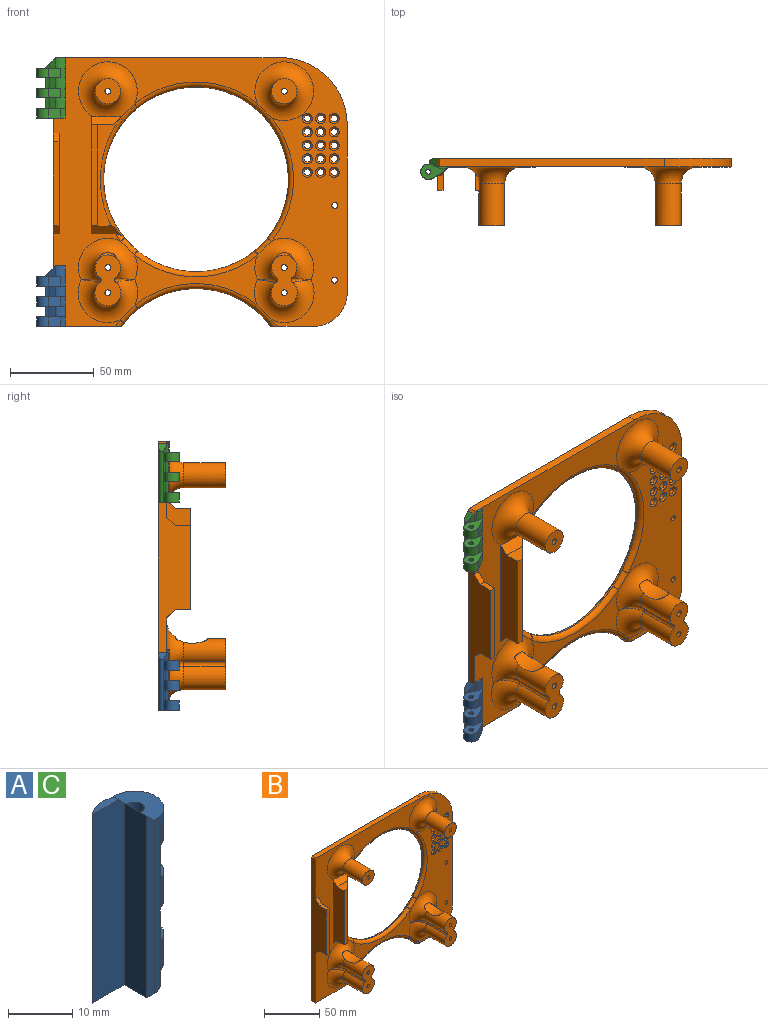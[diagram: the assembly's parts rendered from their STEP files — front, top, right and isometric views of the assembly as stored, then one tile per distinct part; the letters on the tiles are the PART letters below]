
ASSEMBLY  parts=3 mates=2
PART A: 40 faces, bbox 16.8x12.5x36 mm
  f0: plane 34.74x1.74mm, normal (0,-1,0), area 58.9mm2, adj f3,f29,f38,f39
  f1: plane 5.7x2.5mm, normal (-0.71,0.71,0), area 20.2mm2, adj f18,f22,f36,f37
  f2: plane 5.7x2.5mm, normal (-0.71,0.71,0), area 20.2mm2, adj f21,f26,f34,f37
  f3: plane 16.84x12.5mm, normal (0,0,-1), area 102.7mm2, adj f0,f8,f9,f10,f11,f12,f30,f35
  f4: cylinder r=1.5mm len=5.7mm, axis (0,0,1), area 53.7mm2, adj f18,f22
  f5: cylinder r=4.5mm len=9mm, axis (0,0,1), area 94mm2, adj f15,f16,f18,f22
  f6: cylinder r=1.5mm len=5.7mm, axis (0,0,1), area 53.7mm2, adj f21,f26
  f7: cylinder r=4.5mm len=9mm, axis (0,0,1), area 94mm2, adj f13,f14,f21,f26
  f8: cylinder r=1.5mm len=5.7mm, axis (0,0,1), area 53.7mm2, adj f3,f25
  f9: cylinder r=4.5mm len=9mm, axis (0,0,1), area 94mm2, adj f3,f10,f11,f25
  f10: plane 7.27x5.7mm, normal (-0.5,0.87,0), area 47.8mm2, adj f3,f9,f25,f35
  f11: plane 5.7x0.6mm, normal (0,-1,0), area 3.4mm2, adj f3,f9,f12,f25
  f12: plane 30x0.5mm, normal (1,0,0), area 10.6mm2, adj f3,f11,f14,f16,f18,f19,f21,f22
  f13: plane 7.27x5.7mm, normal (-0.5,0.87,0), area 47.8mm2, adj f7,f21,f26,f34
  f14: plane 5.7x0.6mm, normal (0,-1,0), area 3.4mm2, adj f7,f12,f21,f26
  f15: plane 7.27x5.7mm, normal (-0.5,0.87,0), area 47.8mm2, adj f5,f18,f22,f36
  f16: plane 5.7x0.6mm, normal (0,-1,0), area 3.4mm2, adj f5,f12,f18,f22
  f17: plane 5.74x1.45mm, normal (0,0,1), area 6.4mm2, adj f20,f29,f31,f37
  f18: plane 16.84x9.34mm, normal (0,0,1), area 77.8mm2, adj f1,f4,f5,f12,f15,f16,f19,f20
  f19: cylinder r=4.88mm len=2.89mm, axis (0,0,1), area 4.8mm2, adj f12,f18,f20,f29
  f20: plane 6.3x3.46mm, normal (0.43,0.9,0), area 17.8mm2, adj f17,f18,f19,f29,f31
  f21: plane 16.84x9.34mm, normal (0,0,1), area 77.8mm2, adj f2,f6,f7,f12,f13,f14,f23,f24
  f22: plane 16.84x9.34mm, normal (0,0,-1), area 77.8mm2, adj f1,f4,f5,f12,f15,f16,f23,f24
  f23: cylinder r=4.88mm len=6.3mm, axis (0,0,1), area 18.1mm2, adj f12,f21,f22,f24
  f24: plane 6.3x3.46mm, normal (0.43,0.9,0), area 24.2mm2, adj f21,f22,f23,f32
  f25: plane 16.84x9.34mm, normal (0,0,1), area 77.8mm2, adj f8,f9,f10,f11,f12,f27,f28,f30
  f26: plane 16.84x9.34mm, normal (0,0,-1), area 77.8mm2, adj f2,f6,f7,f12,f13,f14,f27,f28
  f27: cylinder r=4.88mm len=6.3mm, axis (0,0,1), area 18.1mm2, adj f12,f25,f26,f28
  f28: plane 6.3x3.46mm, normal (0.43,0.9,0), area 24.2mm2, adj f25,f26,f27,f33
  f29: plane 6x6mm, normal (0.71,0,0.71), area 26.2mm2, adj f0,f12,f17,f19,f20,f37,f38,f39
  f30: plane 5.7x2.5mm, normal (-0.71,0.71,0), area 20.2mm2, adj f3,f25,f35,f37
  f31: cylinder r=5mm len=6.3mm, axis (0,0,1), area 38.7mm2, adj f17,f18,f20,f37
  f32: cylinder r=5mm len=6.3mm, axis (0,0,1), area 38.7mm2, adj f21,f22,f24,f37
  f33: cylinder r=5mm len=6.3mm, axis (0,0,1), area 38.7mm2, adj f25,f26,f28,f37
  f34: cylinder r=5mm len=5.7mm, axis (0,0,-1), area 2.1mm2, adj f2,f13,f21,f26
  f35: cylinder r=5mm len=5.7mm, axis (0,0,-1), area 2.1mm2, adj f3,f10,f25,f30
  f36: cylinder r=5mm len=5.7mm, axis (0,0,-1), area 2.1mm2, adj f1,f15,f18,f22
  f37: plane 36x7mm, normal (0,-1,0), area 251.2mm2, adj f1,f2,f3,f17,f29,f30,f31,f32
  f38: plane 34.74x5mm, normal (-1,0,0), area 173.7mm2, adj f0,f3,f29,f37
  f39: cylinder r=3mm len=33mm, axis (0,0,1), area 146.5mm2, adj f0,f3,f12,f29
PART B: 137 faces, bbox 175.8x40.9x174.3 mm
  f0: plane 175x160mm, normal (0,-1,0), area 8412.6mm2, adj f1,f2,f4,f5,f12,f13,f14,f44
  f1: plane 26.39x5.76mm, normal (0,0,-1), area 125.2mm2, adj f0,f15,f56,f80,f85,f88
  f2: plane 41.39x5.76mm, normal (0,0,-1), area 200.1mm2, adj f0,f12,f15,f56,f84,f85
  f3: plane 73.5x29.9mm, normal (0,-1,0), area 825.3mm2, adj f60,f61,f62,f63,f74,f82
  f4: cylinder r=1.75mm len=3.5mm, axis (0,1,0), area 22mm2, adj f0,f40
  f5: cylinder r=1.75mm len=3.5mm, axis (0,1,0), area 22mm2, adj f0,f38
  f6: cylinder r=1.75mm len=22mm, axis (0,1,0), area 241.9mm2, adj f25,f36
  f7: cylinder r=1.75mm len=22mm, axis (0,1,0), area 241.9mm2, adj f23,f34
  f8: cylinder r=1.75mm len=22mm, axis (0,1,0), area 241.9mm2, adj f19,f32
  f9: cylinder r=1.75mm len=22mm, axis (0,1,0), area 241.9mm2, adj f19,f30
  f10: cylinder r=1.75mm len=22mm, axis (0,1,0), area 241.9mm2, adj f16,f28
  f11: cylinder r=1.75mm len=22mm, axis (0,1,0), area 241.9mm2, adj f16,f26
  f12: plane 158.75x19mm, normal (-1,0,0), area 1518.8mm2, adj f0,f2,f15,f42,f43,f45,f52,f54
  f13: plane 100x5mm, normal (1,0,0), area 500mm2, adj f0,f15,f87,f88
  f14: plane 133.75x5mm, normal (0,0,1), area 668.8mm2, adj f0,f15,f87,f89
  f15: plane 175x160mm, normal (0,1,0), area 15565.5mm2, adj f1,f2,f12,f13,f14,f27,f29,f31
  f16: plane 30.25x15.5mm, normal (0,-1,0), area 350.7mm2, adj f10,f11,f17,f18,f69,f71
  f17: cylinder r=7.75mm len=25mm, axis (0,1,0), area 958.9mm2, adj f16,f60,f69,f71
  f18: cylinder r=7.5mm len=25mm, axis (0,1,0), area 763.3mm2, adj f16,f61,f69,f71,f136
  f19: plane 30.25x15.5mm, normal (0,-1,0), area 350.7mm2, adj f8,f9,f20,f21,f65,f67
  f20: cylinder r=7.75mm len=25mm, axis (0,1,0), area 958.9mm2, adj f19,f62,f65,f67
  f21: cylinder r=7.5mm len=25mm, axis (0,1,0), area 763.3mm2, adj f19,f63,f65,f67,f135
  f22: cylinder r=7.5mm len=25mm, axis (0,1,0), area 1178.1mm2, adj f23,f59
  f23: plane 15x15mm, normal (0,-1,0), area 167.1mm2, adj f7,f22
  f24: cylinder r=7.5mm len=25mm, axis (0,1,0), area 1178.1mm2, adj f25,f58
  f25: plane 15x15mm, normal (0,-1,0), area 167.1mm2, adj f6,f24
  f26: plane 6x6mm, normal (0,1,0), area 18.7mm2, adj f11,f27
  f27: cylinder r=3mm len=18mm, axis (0,1,0), area 339.3mm2, adj f15,f26
  f28: plane 6x6mm, normal (0,1,0), area 18.7mm2, adj f10,f29
  f29: cylinder r=3mm len=18mm, axis (0,1,0), area 339.3mm2, adj f15,f28
  f30: plane 6x6mm, normal (0,1,0), area 18.7mm2, adj f9,f31
  f31: cylinder r=3mm len=18mm, axis (0,1,0), area 339.3mm2, adj f15,f30
  f32: plane 6x6mm, normal (0,1,0), area 18.7mm2, adj f8,f33
  f33: cylinder r=3mm len=18mm, axis (0,1,0), area 339.3mm2, adj f15,f32
  f34: plane 6x6mm, normal (0,1,0), area 18.7mm2, adj f7,f35
  f35: cylinder r=3mm len=18mm, axis (0,1,0), area 339.3mm2, adj f15,f34
  f36: plane 6x6mm, normal (0,1,0), area 18.7mm2, adj f6,f37
  f37: cylinder r=3mm len=18mm, axis (0,1,0), area 339.3mm2, adj f15,f36
  f38: plane 6x6mm, normal (0,1,0), area 18.7mm2, adj f5,f39
  f39: cylinder r=3mm len=6mm, axis (0,1,0), area 56.5mm2, adj f15,f38
  f40: plane 6x6mm, normal (0,1,0), area 18.7mm2, adj f4,f41
  f41: cylinder r=3mm len=6mm, axis (0,1,0), area 56.5mm2, adj f15,f40
  f42: plane 9x3.5mm, normal (0,0,1), area 31.5mm2, adj f12,f44,f45,f52
  f43: plane 9x3.5mm, normal (0,0,-1), area 31.5mm2, adj f12,f44,f45,f54
  f44: plane 60x14mm, normal (1,0,0), area 725mm2, adj f0,f42,f43,f45,f52,f54
  f45: plane 50x3.5mm, normal (0,-1,0), area 175mm2, adj f12,f42,f43,f44
  f46: plane 13.07x9mm, normal (0,0,1), area 77.2mm2, adj f47,f49,f50,f53
  f47: plane 70x14mm, normal (-1,0,0), area 865mm2, adj f0,f46,f48,f49,f51,f53
  f48: plane 12.92x9.02mm, normal (0,0,-1), area 77.1mm2, adj f47,f49,f50,f51,f57
  f49: plane 60x4.07mm, normal (0,-1,0), area 244.3mm2, adj f46,f47,f48,f50
  f50: plane 64.99x13.99mm, normal (0.71,-0.71,0), area 340.1mm2, adj f46,f48,f49,f53,f57,f58
  f51: plane 18.25x6.34mm, normal (0,-0.71,-0.71), area 107.2mm2, adj f0,f47,f48,f57,f72
  f52: plane 5x5mm, normal (0,-0.71,0.71), area 24.7mm2, adj f0,f12,f42,f44
  f53: plane 18.06x5mm, normal (0,-0.71,0.71), area 106.6mm2, adj f0,f46,f47,f50,f58
  f54: plane 5x5mm, normal (0,-0.71,-0.71), area 24.7mm2, adj f0,f12,f43,f44
  f55: cylinder r=55mm len=110mm, axis (0,1,0), area 812.8mm2, adj f57,f72,f73,f74,f75,f76,f77,f78
  f56: cylinder r=55mm len=88.74mm, axis (0,1,0), area 103.2mm2, adj f1,f2,f80,f81,f82,f83,f84,f85
  f57: bspline ~73.3x17.56mm, area 425.2mm2, adj f48,f50,f51,f55,f58,f72,f79
  f58: torus R=17.5mm, axis (0,-1,0), area 1063.5mm2, adj f0,f24,f50,f53,f57,f79
  f59: torus R=17.5mm, axis (0,-1,0), area 1098.9mm2, adj f0,f22,f77
  f60: torus R=17.75mm, axis (0,-1,0), area 792.4mm2, adj f0,f3,f17,f68,f70,f83
  f61: torus R=17.5mm, axis (0,-1,0), area 716.8mm2, adj f0,f3,f18,f68,f70,f73,f136
  f62: torus R=17.75mm, axis (0,-1,0), area 792.4mm2, adj f0,f3,f20,f64,f66,f81
  f63: torus R=17.5mm, axis (0,-1,0), area 716.8mm2, adj f0,f3,f21,f64,f66,f75,f135
  f64: bspline ~13.11x10.57mm, area 21.9mm2, adj f62,f63,f65
  f65: cylinder r=2mm len=25mm, axis (0,-1,0), area 89.3mm2, adj f19,f20,f21,f64
  f66: bspline ~13.11x10.57mm, area 21.9mm2, adj f62,f63,f67
  f67: cylinder r=2mm len=25mm, axis (0,-1,0), area 89.3mm2, adj f19,f20,f21,f66
  f68: bspline ~13.11x10.57mm, area 21.9mm2, adj f60,f61,f69
  f69: cylinder r=2mm len=25mm, axis (0,-1,0), area 89.3mm2, adj f16,f17,f18,f68
  f70: bspline ~13.11x10.57mm, area 21.9mm2, adj f60,f61,f71
  f71: cylinder r=2mm len=25mm, axis (0,-1,0), area 89.3mm2, adj f16,f17,f18,f70
  f72: torus R=58mm, axis (0,-1,0), area 17.6mm2, adj f0,f51,f55,f57,f73
  f73: bspline ~13.46x13.31mm, area 50.2mm2, adj f55,f61,f72,f74
  f74: torus R=58mm, axis (0,-1,0), area 362.8mm2, adj f3,f55,f73,f75
  f75: bspline ~13.46x13.31mm, area 50.2mm2, adj f55,f63,f74,f76
  f76: torus R=58mm, axis (0,-1,0), area 362.8mm2, adj f0,f55,f75,f77
  f77: bspline ~13.46x13.31mm, area 50.2mm2, adj f55,f59,f76,f78
  f78: torus R=58mm, axis (0,-1,0), area 362.8mm2, adj f0,f55,f77,f79
  f79: bspline ~16.65x15.67mm, area 62.6mm2, adj f55,f57,f58,f78
  f80: torus R=58mm, axis (0,-1,0), area 16.7mm2, adj f0,f1,f56,f81
  f81: bspline ~14.19x14.19mm, area 54.8mm2, adj f56,f62,f80,f82
  f82: torus R=58mm, axis (0,-1,0), area 357.6mm2, adj f3,f56,f81,f83
  f83: bspline ~14.19x14.19mm, area 54.8mm2, adj f56,f60,f82,f84
  f84: torus R=58mm, axis (0,-1,0), area 16.7mm2, adj f0,f2,f56,f83
  f85: cone r=55mm half-angle=45deg, axis (0,1,0), area 148.4mm2, adj f1,f2,f15,f56
  f86: cone r=55mm half-angle=45deg, axis (0,1,0), area 493.2mm2, adj f15,f55
  f87: cylinder r=40mm len=40mm, axis (0,1,0), area 314.2mm2, adj f0,f13,f14,f15
  f88: cylinder r=20mm len=20mm, axis (0,-1,0), area 157.1mm2, adj f0,f1,f13,f15
  f89: plane 5x1.25mm, normal (-0.71,0,0.71), area 8.8mm2, adj f0,f12,f14,f15
  f90: cylinder r=2mm len=4mm, axis (0,-1,0), area 37.7mm2, adj f133,f134
  f91: cylinder r=2mm len=4mm, axis (0,-1,0), area 37.7mm2, adj f131,f132
  f92: cylinder r=2mm len=4mm, axis (0,-1,0), area 37.7mm2, adj f129,f130
  f93: cylinder r=2mm len=4mm, axis (0,-1,0), area 37.7mm2, adj f123,f124
  f94: cylinder r=2mm len=4mm, axis (0,-1,0), area 37.7mm2, adj f125,f126
  f95: cylinder r=2mm len=4mm, axis (0,-1,0), area 37.7mm2, adj f127,f128
  f96: cylinder r=2mm len=4mm, axis (0,-1,0), area 37.7mm2, adj f117,f118
  f97: cylinder r=2mm len=4mm, axis (0,-1,0), area 37.7mm2, adj f121,f122
  f98: cylinder r=2mm len=4mm, axis (0,-1,0), area 37.7mm2, adj f111,f112
  f99: cylinder r=2mm len=4mm, axis (0,-1,0), area 37.7mm2, adj f113,f114
  f100: cylinder r=2mm len=4mm, axis (0,-1,0), area 37.7mm2, adj f115,f116
  f101: cylinder r=2mm len=4mm, axis (0,-1,0), area 37.7mm2, adj f119,f120
  f102: cylinder r=2mm len=4mm, axis (0,-1,0), area 37.7mm2, adj f109,f110
  f103: cylinder r=2mm len=4mm, axis (0,-1,0), area 37.7mm2, adj f107,f108
  f104: cylinder r=2mm len=4mm, axis (0,-1,0), area 37.7mm2, adj f105,f106
  f105: cone r=2mm half-angle=45deg, axis (0,-1,0), area 22.2mm2, adj f0,f104
  f106: cone r=2mm half-angle=45deg, axis (0,1,0), area 22.2mm2, adj f15,f104
  f107: cone r=2mm half-angle=45deg, axis (0,-1,0), area 22.2mm2, adj f0,f103
  f108: cone r=2mm half-angle=45deg, axis (0,1,0), area 22.2mm2, adj f15,f103
  f109: cone r=2mm half-angle=45deg, axis (0,-1,0), area 22.2mm2, adj f0,f102
  f110: cone r=2mm half-angle=45deg, axis (0,1,0), area 22.2mm2, adj f15,f102
  f111: cone r=2mm half-angle=45deg, axis (0,-1,0), area 22.2mm2, adj f0,f98
  f112: cone r=2mm half-angle=45deg, axis (0,1,0), area 22.2mm2, adj f15,f98
  f113: cone r=2mm half-angle=45deg, axis (0,-1,0), area 22.2mm2, adj f0,f99
  f114: cone r=2mm half-angle=45deg, axis (0,1,0), area 22.2mm2, adj f15,f99
  f115: cone r=2mm half-angle=45deg, axis (0,-1,0), area 22.2mm2, adj f0,f100
  f116: cone r=2mm half-angle=45deg, axis (0,1,0), area 22.2mm2, adj f15,f100
  f117: cone r=2mm half-angle=45deg, axis (0,-1,0), area 22.2mm2, adj f0,f96
  f118: cone r=2mm half-angle=45deg, axis (0,1,0), area 22.2mm2, adj f15,f96
  f119: cone r=2mm half-angle=45deg, axis (0,-1,0), area 22.2mm2, adj f0,f101
  f120: cone r=2mm half-angle=45deg, axis (0,1,0), area 22.2mm2, adj f15,f101
  f121: cone r=2mm half-angle=45deg, axis (0,-1,0), area 22.2mm2, adj f0,f97
  f122: cone r=2mm half-angle=45deg, axis (0,1,0), area 22.2mm2, adj f15,f97
  f123: cone r=2mm half-angle=45deg, axis (0,-1,0), area 22.2mm2, adj f0,f93
  f124: cone r=2mm half-angle=45deg, axis (0,1,0), area 22.2mm2, adj f15,f93
  f125: cone r=2mm half-angle=45deg, axis (0,-1,0), area 22.2mm2, adj f0,f94
  f126: cone r=2mm half-angle=45deg, axis (0,1,0), area 22.2mm2, adj f15,f94
  f127: cone r=2mm half-angle=45deg, axis (0,-1,0), area 22.2mm2, adj f0,f95
  f128: cone r=2mm half-angle=45deg, axis (0,1,0), area 22.2mm2, adj f15,f95
  f129: cone r=2mm half-angle=45deg, axis (0,-1,0), area 22.2mm2, adj f0,f92
  f130: cone r=2mm half-angle=45deg, axis (0,1,0), area 22.2mm2, adj f15,f92
  f131: cone r=2mm half-angle=45deg, axis (0,-1,0), area 22.2mm2, adj f0,f91
  f132: cone r=2mm half-angle=45deg, axis (0,1,0), area 22.2mm2, adj f15,f91
  f133: cone r=2mm half-angle=45deg, axis (0,-1,0), area 22.2mm2, adj f0,f90
  f134: cone r=2mm half-angle=45deg, axis (0,1,0), area 22.2mm2, adj f15,f90
  f135: extruded ~19.26x11.18mm, area 198.1mm2, adj f21,f63
  f136: extruded ~19.26x11.18mm, area 198.1mm2, adj f18,f61
PART C: same geometry as A
PLACE A rot(axis=(0,0,-1),180deg) t=(-107.98,-22.63,-48.37)mm
PLACE B t=(-32.64,-18.63,-4.37)mm fixed
PLACE C rot(axis=(0,0,1),180deg) t=(-107.98,-22.63,75.63)mm
MATE planar A.f3 <-> B.f2  axis (0,0,-1) through (-117.64,-21.13,-84.37)mm
MATE cylindrical A.f4 <-> C.f4  axis (0,0,1) through (-122.98,-26.63,-54.67)mm
